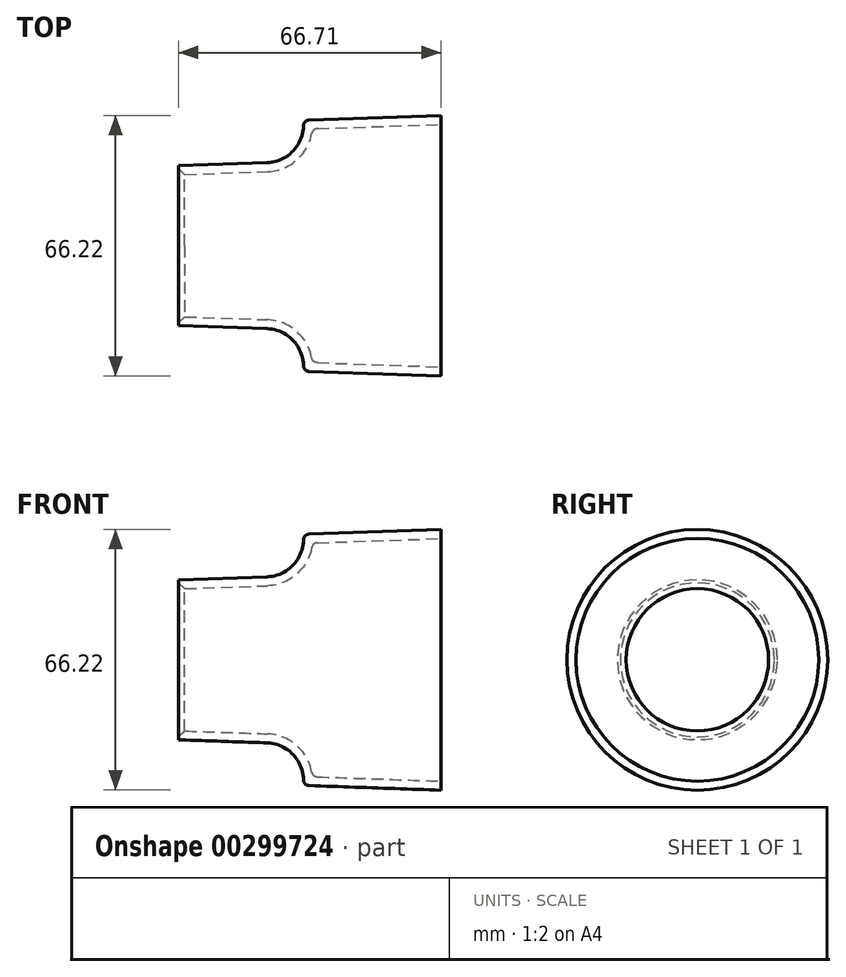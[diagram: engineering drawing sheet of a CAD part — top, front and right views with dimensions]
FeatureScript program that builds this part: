
annotation { "Feature Type Name" : "Feature", "Feature Type Description" : "" }
export const myFeature = defineFeature(function(context is Context, id is Id, definition is map)
    precondition{}
    {
        {
            var Q0;
            Q0=qCreatedBy(makeId("Front.planeOp"),FACE);
            var sketch = newSketch(context, id + "F0", { "sketchPlane" : qUnion([Q0])});
            skLineSegment(sketch, "E0", {"start": v(-33.12, 0) * mm, "end": v(39.78, 0) * mm, "construction": true});
            skLineSegment(sketch, "E1", {"start": v(-28.28, 20.32) * mm, "end": v(-5.74, 21.1) * mm});
            skLineSegment(sketch, "E2", {"start": v(3.45, 30.63) * mm, "end": v(3.45, 31.9) * mm});
            skLineSegment(sketch, "E3", {"start": v(3.45, 31.9) * mm, "end": v(38.35, 33.11) * mm});
            skPoint(sketch, "E4.visualSharp", {"position": v(3.45, 21.43) * mm});
            skArc(sketch, "E4.filletArc", {"start": v(-5.74, 21.1) * mm, "mid": v(0.78, 24) * mm, "end": v(3.45, 30.63) * mm});
            skLineSegment(sketch, "E5.0", {"start": v(-28.2, 18.04) * mm, "end": v(-5.66, 18.82) * mm});
            skArc(sketch, "E6.0", {"start": v(-5.66, 18.82) * mm, "mid": v(2.09, 22.09) * mm, "end": v(5.7, 29.68) * mm});
            skLineSegment(sketch, "E7.0", {"start": v(5.7, 29.68) * mm, "end": v(38.43, 30.83) * mm});
            skLineSegment(sketch, "E8", {"start": v(38.35, 33.11) * mm, "end": v(38.43, 30.83) * mm});
            skLineSegment(sketch, "E9", {"start": v(-28.28, 20.32) * mm, "end": v(-28.2, 18.04) * mm});
            skSolve(sketch);
        }
        {
            var Q0;
            Q0=makeQuery(id+"F0.imprint","IMPRINT",FACE,{"disambiguationData":[TD([[makeQuery(id+"F0.imprint","IMPRINT",EDGE,{"derivedFrom":sQuery(id+"F0.wireOp",EDGE,"E1")}),-1.0]])]});
            var Q1;
            Q1=sQuery(id+"F0.wireOp",EDGE,"E0");
            revolve(context, id + "F1", {"entities" : qUnion([Q0]), "axis" : qUnion([Q1]), "revolveType" : RevolveType.FULL, "oppositeDirection" : true});
        }
        {
            var Q0;
            Q0=makeQuery(id+"F1.opRevolve","SWEPT_EDGE",EDGE,{"disambiguationData":[OSD([sQuery(id+"F0.wireOp",EDGE,"E2"),sQuery(id+"F0.wireOp",EDGE,"E3")])]});
            fillet(context, id + "F2", {"entities" : qUnion([Q0]), "radius" : 1.52 * mm, "tangentPropagation" : true, "allowEdgeOverflow" : false});
        }
        {
            var Q0;
            Q0=makeQuery(id+"F1.opRevolve","SWEPT_EDGE",EDGE,{"disambiguationData":[OSD([sQuery(id+"F0.wireOp",EDGE,"E6.0"),sQuery(id+"F0.wireOp",EDGE,"E7.0")])]});
            fillet(context, id + "F3", {"entities" : qUnion([Q0]), "radius" : 1.52 * mm, "tangentPropagation" : true, "allowEdgeOverflow" : false});
        }
        {
            var Q0;
            Q0=makeQuery(id+"F1.opRevolve","SWEPT_EDGE",EDGE,{"disambiguationData":[OSD([sQuery(id+"F0.wireOp",EDGE,"E5.0"),sQuery(id+"F0.wireOp",EDGE,"E9")])]});
            chamfer(context, id + "F4", {"entities" : qUnion([Q0]), "width" : 1.52 * mm, "tangentPropagation" : true});
        }
    });
